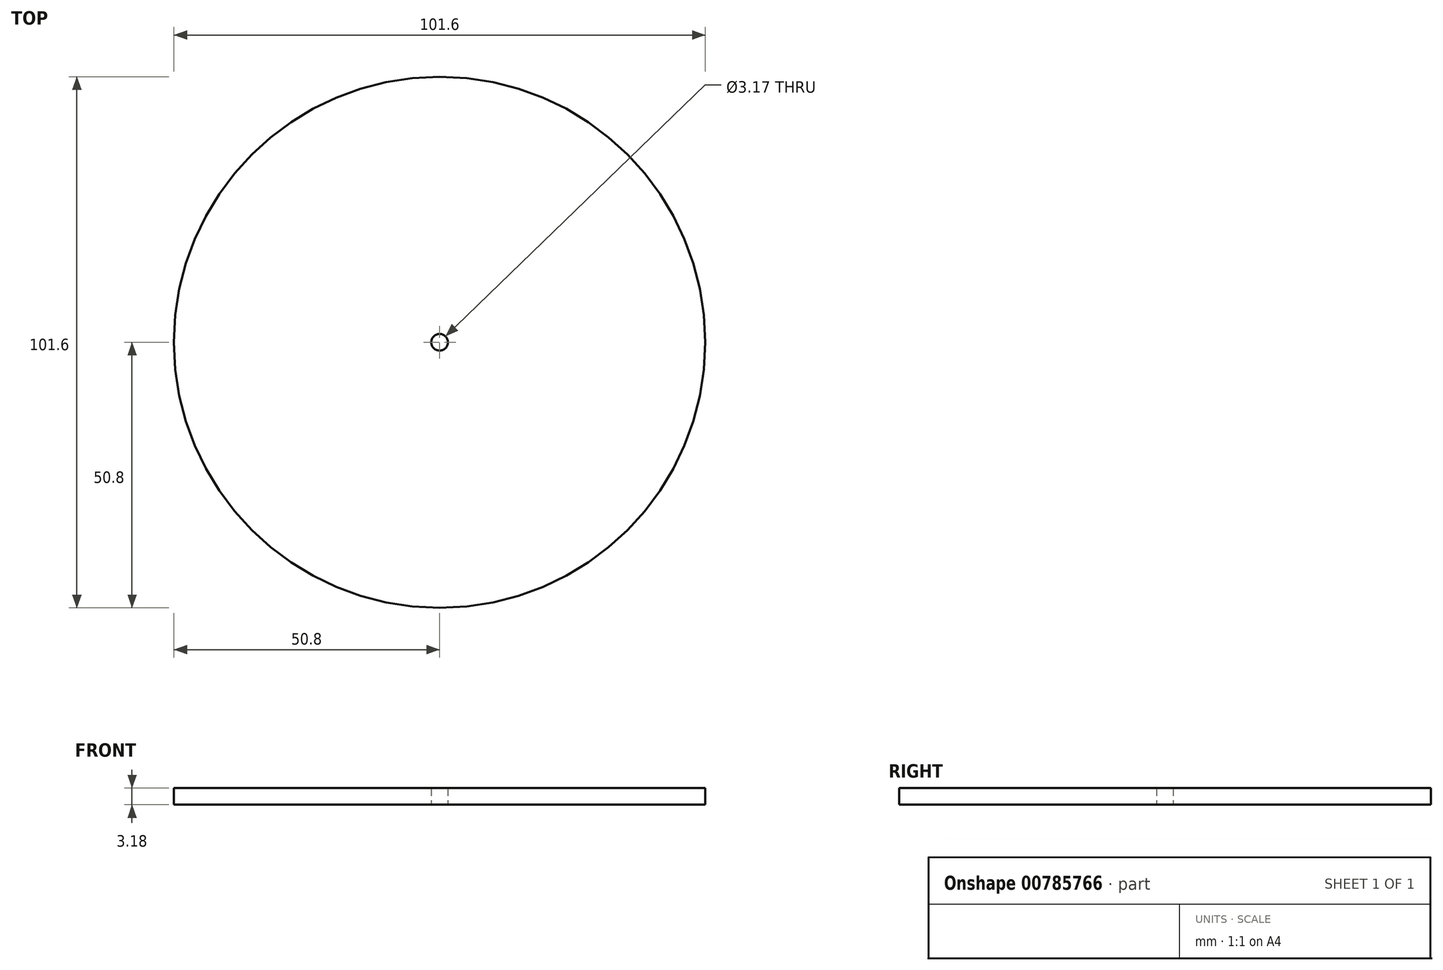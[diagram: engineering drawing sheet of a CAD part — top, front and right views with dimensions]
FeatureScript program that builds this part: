
annotation { "Feature Type Name" : "Feature", "Feature Type Description" : "" }
export const myFeature = defineFeature(function(context is Context, id is Id, definition is map)
    precondition{}
    {
        {
            var Q0;
            Q0=qCreatedBy(makeId("Top.planeOp"),FACE);
            var sketch = newSketch(context, id + "F0", { "sketchPlane" : qUnion([Q0])});
            skCircle(sketch, "E0", {"center": v(0, 0) * mm, "radius": 50.8 * mm});
            skCircle(sketch, "E1", {"center": v(0, 0) * mm, "radius": 1.59 * mm});
            skSolve(sketch);
        }
        {
            var Q0;
            Q0=makeQuery(id+"F0.imprint","IMPRINT",FACE,{"disambiguationData":[TD([[makeQuery(id+"F0.imprint","IMPRINT",EDGE,{"derivedFrom":sQuery(id+"F0.wireOp",EDGE,"E0")}),1.0]])]});
            extrude(context, id + "F1", {"entities" : qUnion([Q0]), "depth" : 3.17 * mm, "offsetDistance" : 25.4 * mm});
        }
    });
